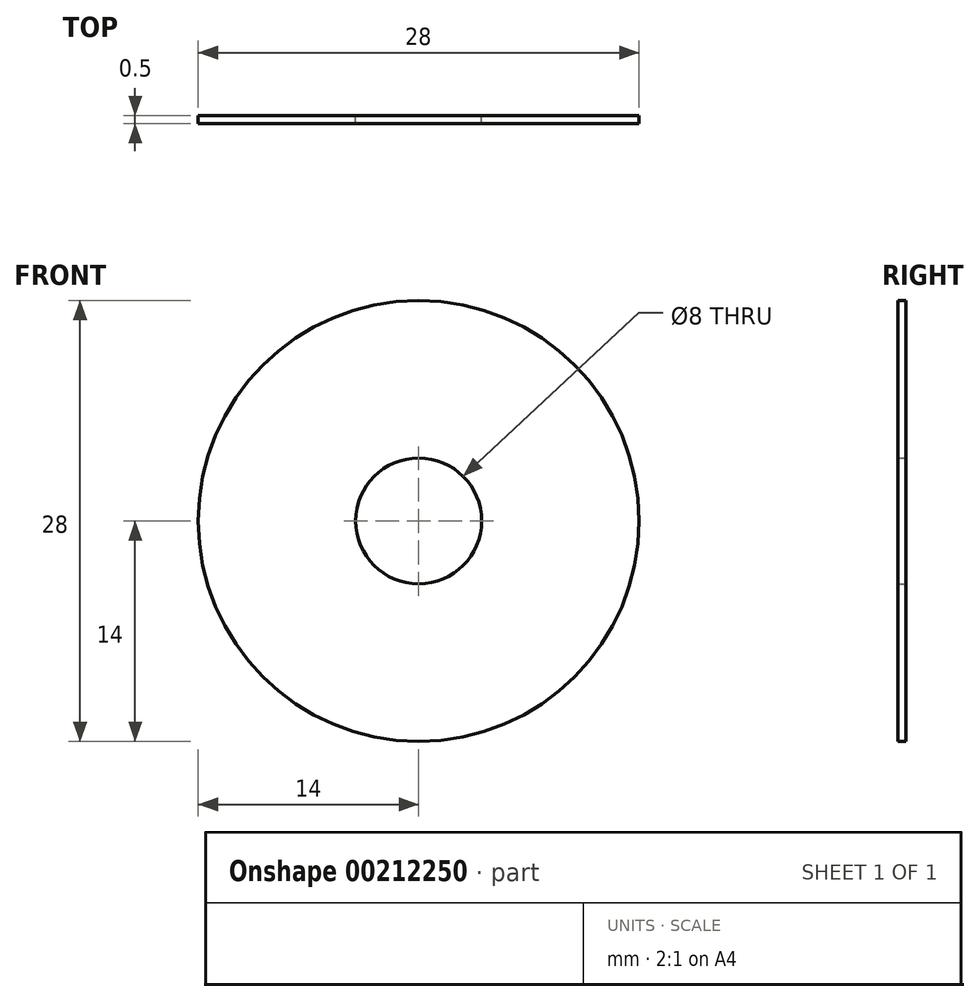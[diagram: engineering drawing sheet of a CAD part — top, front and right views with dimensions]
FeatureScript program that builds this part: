
annotation { "Feature Type Name" : "Feature", "Feature Type Description" : "" }
export const myFeature = defineFeature(function(context is Context, id is Id, definition is map)
    precondition{}
    {
        {
            var Q0;
            Q0=qCreatedBy(makeId("Front.planeOp"),FACE);
            var sketch = newSketch(context, id + "F0", { "sketchPlane" : qUnion([Q0])});
            skCircle(sketch, "E0", {"center": v(0, 0) * mm, "radius": 14 * mm});
            skCircle(sketch, "E1", {"center": v(0, 0) * mm, "radius": 4 * mm});
            skSolve(sketch);
        }
        {
            var Q0;
            Q0=makeQuery(id+"F0.imprint","IMPRINT",FACE,{"disambiguationData":[TD([[makeQuery(id+"F0.imprint","IMPRINT",EDGE,{"derivedFrom":sQuery(id+"F0.wireOp",EDGE,"E0")}),1.0]])]});
            extrude(context, id + "F1", {"entities" : qUnion([Q0]), "depth" : 0.5 * mm});
        }
    });
